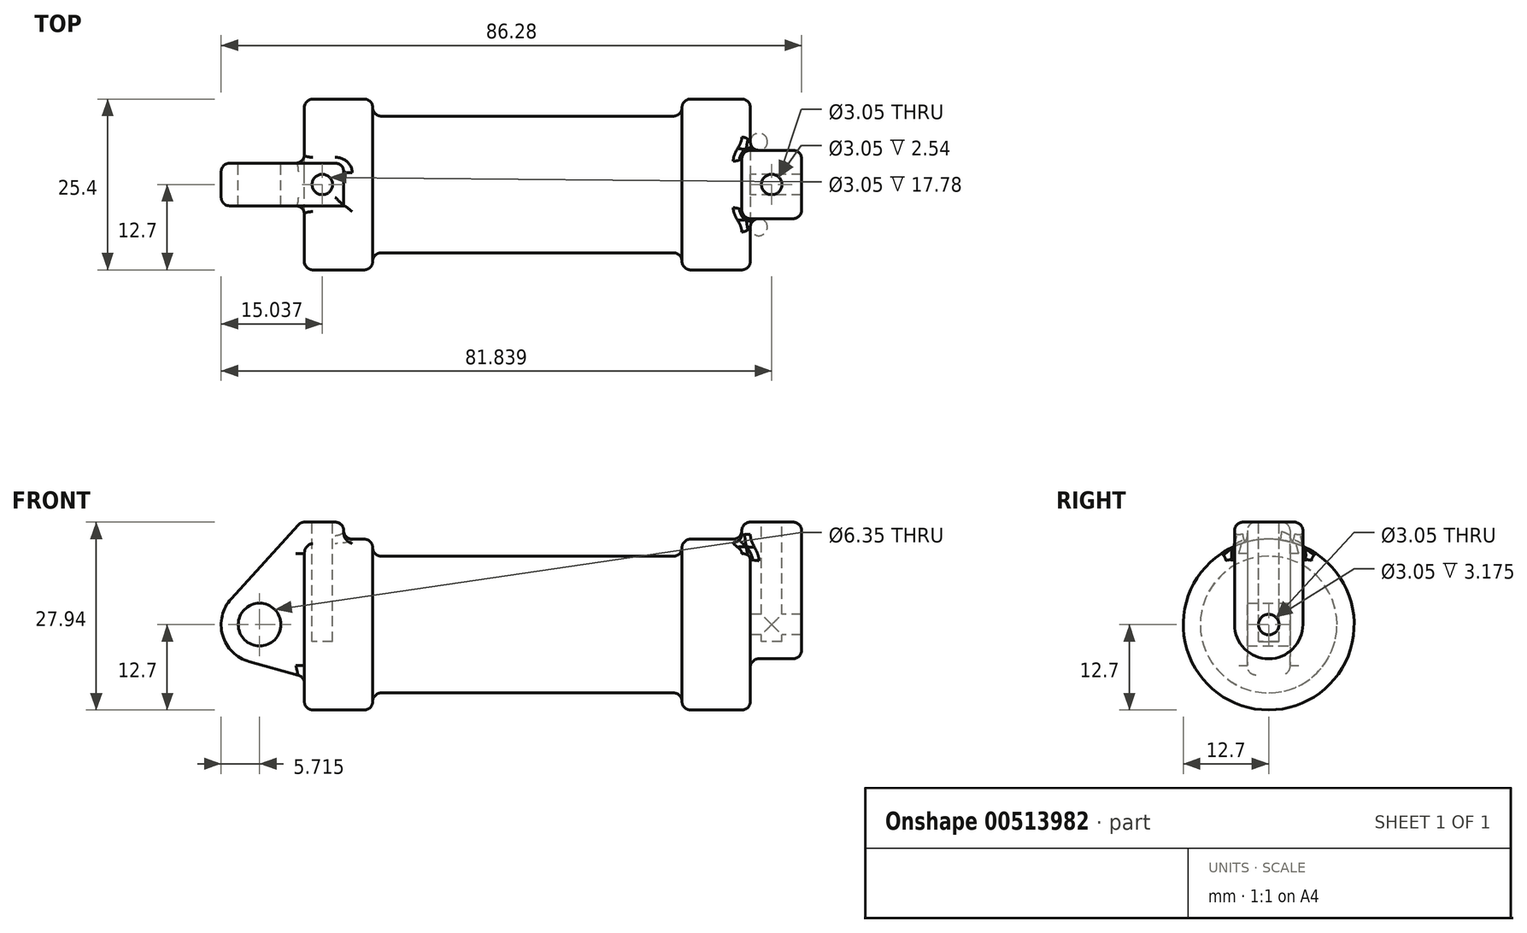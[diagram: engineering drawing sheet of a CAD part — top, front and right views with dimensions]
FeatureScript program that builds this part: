
annotation { "Feature Type Name" : "Feature", "Feature Type Description" : "" }
export const myFeature = defineFeature(function(context is Context, id is Id, definition is map)
    precondition{}
    {
        {
            var Q0;
            Q0=qCreatedBy(makeId("Front.planeOp"),FACE);
            var sketch = newSketch(context, id + "F0", { "sketchPlane" : qUnion([Q0])});
            skLineSegment(sketch, "E0", {"start": v(0, 0) * mm, "end": v(0, 12.7) * mm});
            skLineSegment(sketch, "E1", {"start": v(0, 12.7) * mm, "end": v(10.16, 12.7) * mm});
            skLineSegment(sketch, "E2", {"start": v(10.16, 12.7) * mm, "end": v(10.16, 10.16) * mm});
            skLineSegment(sketch, "E3", {"start": v(10.16, 10.16) * mm, "end": v(56.13, 10.16) * mm});
            skLineSegment(sketch, "E4", {"start": v(56.13, 10.16) * mm, "end": v(56.13, 12.7) * mm});
            skLineSegment(sketch, "E5", {"start": v(56.13, 12.7) * mm, "end": v(66.3, 12.7) * mm});
            skLineSegment(sketch, "E6", {"start": v(66.3, 12.7) * mm, "end": v(66.3, 0) * mm});
            skLineSegment(sketch, "E7", {"start": v(66.3, 0) * mm, "end": v(0, 0) * mm});
            skLineSegment(sketch, "E8", {"start": v(5.84, 15.24) * mm, "end": v(-0.5, 15.24) * mm});
            skLineSegment(sketch, "E9", {"start": v(-0.5, 15.24) * mm, "end": v(-10.88, 3.85) * mm});
            skLineSegment(sketch, "E10", {"start": v(0, 0) * mm, "end": v(-6.65, 0) * mm});
            skCircle(sketch, "E11", {"center": v(-6.65, 0) * mm, "radius": 5.72 * mm});
            skCircle(sketch, "E12", {"center": v(-6.65, 0) * mm, "radius": 3.18 * mm});
            skLineSegment(sketch, "E13", {"start": v(5.84, 15.24) * mm, "end": v(5.84, -9.4) * mm});
            skLineSegment(sketch, "E14", {"start": v(5.84, -9.4) * mm, "end": v(-8.18, -5.5) * mm});
            skSolve(sketch);
        }
        {
            var Q0;
            {var subQ0=sQuery(id+"F0.wireOp",EDGE,"E2");Q0=makeQuery(id+"F0.imprint","IMPRINT",FACE,{"disambiguationData":[TD([[makeQuery(id+"F0.imprint","IMPRINT",EDGE,{"derivedFrom":subQ0}),-1.0]])]});}
            var Q1;
            {var subQ0=sQuery(id+"F0.wireOp",EDGE,"E0");Q1=makeQuery(id+"F0.imprint","IMPRINT",FACE,{"disambiguationData":[TD([[makeQuery(id+"F0.imprint","IMPRINT",EDGE,{"derivedFrom":subQ0}),-1.0]])]});}
            var Q2;
            Q2=sQuery(id+"F0.wireOp",EDGE,"E7");
            revolve(context, id + "F1", {"entities" : qUnion([Q0, Q1]), "axis" : qUnion([Q2]), "revolveType" : RevolveType.FULL});
        }
        {
            var Q0;
            {var subQ1=sQuery(id+"F0.wireOp",EDGE,"E0");Q0=makeQuery(id+"F0.imprint","IMPRINT",FACE,{"disambiguationData":[TD([[makeQuery(id+"F0.imprint","IMPRINT",EDGE,{"derivedFrom":subQ1}),1.0]])]});}
            var Q1;
            {var subQ5=sQuery(id+"F0.wireOp",EDGE,"E12");Q1=makeQuery(id+"F0.imprint","IMPRINT",FACE,{"disambiguationData":[TD([[makeQuery(id+"F0.imprint","IMPRINT",EDGE,{"derivedFrom":subQ5}),-1.0]])]});}
            var Q2;
            {var subQ0=sQuery(id+"F0.wireOp",EDGE,"E14");Q2=makeQuery(id+"F0.imprint","IMPRINT",FACE,{"disambiguationData":[TD([[makeQuery(id+"F0.imprint","IMPRINT",EDGE,{"derivedFrom":subQ0}),-1.0]])]});}
            var Q3;
            {var subQ0=sQuery(id+"F0.wireOp",EDGE,"E0");Q3=makeQuery(id+"F0.imprint","IMPRINT",FACE,{"disambiguationData":[TD([[makeQuery(id+"F0.imprint","IMPRINT",EDGE,{"derivedFrom":subQ0}),-1.0]])]});}
            extrude(context, id + "F2", {"entities" : qUnion([Q0, Q1, Q2, Q3]), "operationType" : NewBodyOperationType.ADD, "endBound" : BoundingType.SYMMETRIC, "depth" : 6.35 * mm, "offsetDistance" : 25.4 * mm});
        }
        {
            var Q0;
            Q0=makeQuery(id+"F1.opRevolve","SWEPT_FACE",FACE,{"disambiguationData":[OSD([sQuery(id+"F0.wireOp",EDGE,"E6")])]});
            var sketch = newSketch(context, id + "F3", { "sketchPlane" : qUnion([Q0])});
            skCircle(sketch, "E15", {"center": v(0, 0) * mm, "radius": 1.52 * mm});
            skCircle(sketch, "E16", {"center": v(0, 0) * mm, "radius": 5.08 * mm});
            skLineSegment(sketch, "E17", {"start": v(5.08, 0) * mm, "end": v(5.08, 15.24) * mm});
            skLineSegment(sketch, "E18", {"start": v(-5.08, 0) * mm, "end": v(-5.08, 15.24) * mm});
            skLineSegment(sketch, "E19", {"start": v(-5.08, 15.24) * mm, "end": v(5.08, 15.24) * mm});
            skSolve(sketch);
        }
        {
            var Q0;
            Q0=makeQuery(id+"F3.imprint","IMPRINT",FACE,{"disambiguationData":[TD([[makeQuery(id+"F3.imprint","IMPRINT",EDGE,{"derivedFrom":sQuery(id+"F3.wireOp",EDGE,"E15")}),-1.0]])]});
            var Q1;
            {var subQ0=sQuery(id+"F3.wireOp",EDGE,"E17");var subQ1=sQuery(id+"F3.wireOp",EDGE,"E16");var subQ2=makeQuery(id+"F3.imprint","INTERSECT",VERTEX,{"derivedFrom":[subQ1,subQ0]});Q1=makeQuery(id+"F3.imprint","IMPRINT",FACE,{"disambiguationData":[TD([[makeQuery(id+"F3.imprint","IMPRINT",EDGE,{"disambiguationData":[TD([[subQ2,-1.0]])],"derivedFrom":subQ1}),-1.0]])]});}
            var Q2;
            {var subQ0=sQuery(id+"F3.wireOp",EDGE,"E19");Q2=makeQuery(id+"F3.imprint","IMPRINT",FACE,{"disambiguationData":[TD([[makeQuery(id+"F3.imprint","IMPRINT",EDGE,{"derivedFrom":subQ0}),-1.0]])]});}
            extrude(context, id + "F4", {"entities" : qUnion([Q0, Q1, Q2]), "operationType" : NewBodyOperationType.ADD, "depth" : 7.62 * mm, "hasSecondDirection" : true, "secondDirectionOppositeDirection" : true, "secondDirectionDepth" : 1.27 * mm});
        }
        {
            var Q0;
            Q0=makeQuery(id+"F2.opExtrude","SWEPT_FACE",FACE,{"disambiguationData":[OSD([sQuery(id+"F0.wireOp",EDGE,"E8")])]});
            var sketch = newSketch(context, id + "F5", { "sketchPlane" : qUnion([Q0])});
            skCircle(sketch, "E20", {"center": v(2.67, 0) * mm, "radius": 1.52 * mm});
            skPoint(sketch, "E21.0", {"position": v(65.02, 0) * mm});
            skPoint(sketch, "E22.0", {"position": v(69.47, 5.08) * mm});
            skCircle(sketch, "E23", {"center": v(69.47, 0) * mm, "radius": 1.52 * mm});
            skSolve(sketch);
        }
        {
            var Q0;
            Q0=makeQuery(id+"F5.imprint","IMPRINT",FACE,{"disambiguationData":[TD([[makeQuery(id+"F5.imprint","IMPRINT",EDGE,{"derivedFrom":sQuery(id+"F5.wireOp",EDGE,"E23")}),1.0]])]});
            var Q1;
            Q1=sQuery(id+"F5.wireOp",EDGE,"E20");
            extrude(context, id + "F6", {"entities" : qUnion([Q0]), "operationType" : NewBodyOperationType.REMOVE, "surfaceEntities" : qUnion([Q1]), "oppositeDirection" : true, "depth" : 10.4 * mm});
        }
        {
            var Q0;
            Q0 = qSketchRegion(id + "F5", true);
            extrude(context, id + "F7", {"entities" : qUnion([Q0]), "operationType" : NewBodyOperationType.REMOVE, "oppositeDirection" : true, "depth" : 17.78 * mm});
        }
        {
            var Q0;
            Q0=makeQuery(id+"F1.opRevolve","SWEPT_FACE",FACE,{"disambiguationData":[OSD([sQuery(id+"F0.wireOp",EDGE,"E4")])]});
            fillet(context, id + "F8", {"entities" : qUnion([Q0]), "radius" : 1.27 * mm, "tangentPropagation" : true, "allowEdgeOverflow" : false});
        }
        {
            var Q0;
            Q0=makeQuery(id+"F1.opRevolve","SWEPT_FACE",FACE,{"disambiguationData":[OSD([sQuery(id+"F0.wireOp",EDGE,"E2")])]});
            fillet(context, id + "F9", {"entities" : qUnion([Q0]), "radius" : 1.27 * mm, "tangentPropagation" : true, "allowEdgeOverflow" : false});
        }
        {
            var Q0;
            Q0=makeQuery(id+"F1.opRevolve","SWEPT_EDGE",EDGE,{"disambiguationData":[OSD([sQuery(id+"F0.wireOp",EDGE,"E0"),sQuery(id+"F0.wireOp",EDGE,"E1")])]});
            var Q1;
            Q1=makeQuery(id+"F2.boolean.opBoolean","INTERSECT",EDGE,{"derivedFrom":[makeQuery(id+"F1.opRevolve","SWEPT_FACE",FACE,{"disambiguationData":[OSD([sQuery(id+"F0.wireOp",EDGE,"E0")])]}),makeQuery(id+"F2.opExtrude","CAP_FACE",FACE,{"disambiguationData":[OSD([sQuery(id+"F0.wireOp",EDGE,"E8"),sQuery(id+"F0.wireOp",EDGE,"E9"),sQuery(id+"F0.wireOp",EDGE,"E11"),sQuery(id+"F0.wireOp",EDGE,"E12"),sQuery(id+"F0.wireOp",EDGE,"E13"),sQuery(id+"F0.wireOp",EDGE,"E14")])],"isStart":true})]});
            var Q2;
            {var subQ0=sQuery(id+"F0.wireOp",EDGE,"E1");Q2=makeQuery(id+"F9.opFillet","BLEND_EDGE",EDGE,{"blendedFrom":[makeQuery(id+"F1.opRevolve","SWEPT_EDGE",EDGE,{"disambiguationData":[OSD([subQ0,sQuery(id+"F0.wireOp",EDGE,"E2")])]}),makeQuery(id+"F1.opRevolve","SWEPT_FACE",FACE,{"disambiguationData":[OSD([subQ0])]})],"blendedInto":[makeQuery(id+"F1.opRevolve","SWEPT_FACE",FACE,{"disambiguationData":[OSD([subQ0])]})]});}
            var Q3;
            Q3=makeQuery(id+"F1.opRevolve","SWEPT_FACE",FACE,{"disambiguationData":[OSD([sQuery(id+"F0.wireOp",EDGE,"E1")])]});
            var Q4;
            Q4=makeQuery(id+"F2.opExtrude","CAP_EDGE",EDGE,{"disambiguationData":[OSD([sQuery(id+"F0.wireOp",EDGE,"E13")])],"isStart":true});
            var Q5;
            Q5=makeQuery(id+"F2.boolean.opBoolean","INTERSECT",EDGE,{"derivedFrom":[makeQuery(id+"F1.opRevolve","SWEPT_FACE",FACE,{"disambiguationData":[OSD([sQuery(id+"F0.wireOp",EDGE,"E1")])]}),makeQuery(id+"F2.opExtrude","CAP_FACE",FACE,{"disambiguationData":[OSD([sQuery(id+"F0.wireOp",EDGE,"E8"),sQuery(id+"F0.wireOp",EDGE,"E9"),sQuery(id+"F0.wireOp",EDGE,"E11"),sQuery(id+"F0.wireOp",EDGE,"E12"),sQuery(id+"F0.wireOp",EDGE,"E13"),sQuery(id+"F0.wireOp",EDGE,"E14")])],"isStart":true})]});
            var Q6;
            Q6=makeQuery(id+"F2.opExtrude","CAP_EDGE",EDGE,{"disambiguationData":[OSD([sQuery(id+"F0.wireOp",EDGE,"E8")])],"isStart":true});
            var Q7;
            Q7=makeQuery(id+"F2.opExtrude","CAP_EDGE",EDGE,{"disambiguationData":[OSD([sQuery(id+"F0.wireOp",EDGE,"E9")])],"isStart":true});
            var Q8;
            Q8=makeQuery(id+"F2.opExtrude","CAP_EDGE",EDGE,{"disambiguationData":[OSD([sQuery(id+"F0.wireOp",EDGE,"E11")])],"isStart":true});
            var Q9;
            Q9=makeQuery(id+"F2.opExtrude","SWEPT_EDGE",EDGE,{"disambiguationData":[OSD([sQuery(id+"F0.wireOp",EDGE,"E9"),sQuery(id+"F0.wireOp",EDGE,"E11")])]});
            var Q10;
            Q10=makeQuery(id+"F2.opExtrude","CAP_EDGE",EDGE,{"disambiguationData":[OSD([sQuery(id+"F0.wireOp",EDGE,"E9")])],"isStart":false});
            var Q11;
            Q11=makeQuery(id+"F2.opExtrude","SWEPT_EDGE",EDGE,{"disambiguationData":[OSD([sQuery(id+"F0.wireOp",EDGE,"E8"),sQuery(id+"F0.wireOp",EDGE,"E9")])]});
            var Q12;
            Q12=makeQuery(id+"F2.opExtrude","CAP_EDGE",EDGE,{"disambiguationData":[OSD([sQuery(id+"F0.wireOp",EDGE,"E8")])],"isStart":false});
            var Q13;
            Q13=makeQuery(id+"F2.opExtrude","SWEPT_EDGE",EDGE,{"disambiguationData":[OSD([sQuery(id+"F0.wireOp",EDGE,"E8"),sQuery(id+"F0.wireOp",EDGE,"E13")])]});
            var Q14;
            Q14=makeQuery(id+"F2.opExtrude","CAP_EDGE",EDGE,{"disambiguationData":[OSD([sQuery(id+"F0.wireOp",EDGE,"E11")])],"isStart":false});
            var Q15;
            Q15=makeQuery(id+"F2.opExtrude","CAP_EDGE",EDGE,{"disambiguationData":[OSD([sQuery(id+"F0.wireOp",EDGE,"E14")])],"isStart":false});
            var Q16;
            Q16=makeQuery(id+"F2.boolean.opBoolean","INTERSECT",EDGE,{"derivedFrom":[makeQuery(id+"F1.opRevolve","SWEPT_FACE",FACE,{"disambiguationData":[OSD([sQuery(id+"F0.wireOp",EDGE,"E0")])]}),makeQuery(id+"F2.opExtrude","CAP_FACE",FACE,{"disambiguationData":[OSD([sQuery(id+"F0.wireOp",EDGE,"E8"),sQuery(id+"F0.wireOp",EDGE,"E9"),sQuery(id+"F0.wireOp",EDGE,"E11"),sQuery(id+"F0.wireOp",EDGE,"E12"),sQuery(id+"F0.wireOp",EDGE,"E13"),sQuery(id+"F0.wireOp",EDGE,"E14")])],"isStart":false})]});
            var Q17;
            Q17=makeQuery(id+"F2.opExtrude","CAP_EDGE",EDGE,{"disambiguationData":[OSD([sQuery(id+"F0.wireOp",EDGE,"E14")])],"isStart":true});
            var Q18;
            Q18=makeQuery(id+"F2.boolean.opBoolean","INTERSECT",EDGE,{"derivedFrom":[makeQuery(id+"F1.opRevolve","SWEPT_FACE",FACE,{"disambiguationData":[OSD([sQuery(id+"F0.wireOp",EDGE,"E0")])]}),makeQuery(id+"F2.opExtrude","SWEPT_FACE",FACE,{"disambiguationData":[OSD([sQuery(id+"F0.wireOp",EDGE,"E14")])]})]});
            fillet(context, id + "F10", {"entities" : qUnion([Q0, Q1, Q2, Q3, Q4, Q5, Q6, Q7, Q8, Q9, Q10, Q11, Q12, Q13, Q14, Q15, Q16, Q17, Q18]), "radius" : 1.27 * mm, "tangentPropagation" : true, "allowEdgeOverflow" : false});
        }
        {
            var Q0;
            Q0=makeQuery(id+"F4.opExtrude","SWEPT_EDGE",EDGE,{"disambiguationData":[OSD([sQuery(id+"F3.wireOp",EDGE,"E17"),sQuery(id+"F3.wireOp",EDGE,"E19")])]});
            var Q1;
            Q1=makeQuery(id+"F4.opExtrude","SWEPT_EDGE",EDGE,{"disambiguationData":[OSD([sQuery(id+"F3.wireOp",EDGE,"E18"),sQuery(id+"F3.wireOp",EDGE,"E19")])]});
            var Q2;
            Q2=makeQuery(id+"F4.opExtrude","CAP_EDGE",EDGE,{"disambiguationData":[OSD([sQuery(id+"F3.wireOp",EDGE,"E19")])],"isStart":false});
            var Q3;
            Q3=makeQuery(id+"F4.opExtrude","CAP_EDGE",EDGE,{"disambiguationData":[OSD([sQuery(id+"F3.wireOp",EDGE,"E19")])],"isStart":true});
            var Q4;
            Q4=makeQuery(id+"F4.opExtrude","CAP_EDGE",EDGE,{"disambiguationData":[OSD([sQuery(id+"F3.wireOp",EDGE,"E17")])],"isStart":true});
            var Q5;
            Q5=makeQuery(id+"F4.boolean.opBoolean","INTERSECT",EDGE,{"derivedFrom":[makeQuery(id+"F1.opRevolve","SWEPT_FACE",FACE,{"disambiguationData":[OSD([sQuery(id+"F0.wireOp",EDGE,"E5")])]}),makeQuery(id+"F4.opExtrude","CAP_FACE",FACE,{"disambiguationData":[OSD([sQuery(id+"F3.wireOp",EDGE,"E15"),sQuery(id+"F3.wireOp",EDGE,"E16"),sQuery(id+"F3.wireOp",EDGE,"E17"),sQuery(id+"F3.wireOp",EDGE,"E18"),sQuery(id+"F3.wireOp",EDGE,"E19")])],"isStart":true})]});
            var Q6;
            Q6=makeQuery(id+"F4.opExtrude","CAP_EDGE",EDGE,{"disambiguationData":[OSD([sQuery(id+"F3.wireOp",EDGE,"E18")])],"isStart":true});
            var Q7;
            Q7=makeQuery(id+"F4.opExtrude","CAP_EDGE",EDGE,{"disambiguationData":[OSD([sQuery(id+"F3.wireOp",EDGE,"E17")])],"isStart":false});
            var Q8;
            Q8=makeQuery(id+"F4.opExtrude","CAP_EDGE",EDGE,{"disambiguationData":[OSD([sQuery(id+"F3.wireOp",EDGE,"E18")])],"isStart":false});
            var Q9;
            Q9=makeQuery(id+"F4.opExtrude","CAP_EDGE",EDGE,{"disambiguationData":[OSD([sQuery(id+"F3.wireOp",EDGE,"E16")])],"isStart":false});
            var Q10;
            Q10=makeQuery(id+"F4.boolean.opBoolean","INTERSECT",EDGE,{"derivedFrom":[makeQuery(id+"F1.opRevolve","SWEPT_FACE",FACE,{"disambiguationData":[OSD([sQuery(id+"F0.wireOp",EDGE,"E6")])]}),makeQuery(id+"F4.opExtrude","SWEPT_FACE",FACE,{"disambiguationData":[OSD([sQuery(id+"F3.wireOp",EDGE,"E16")])]})]});
            var Q11;
            Q11=makeQuery(id+"F4.opExtrude","SWEPT_EDGE",EDGE,{"disambiguationData":[OSD([sQuery(id+"F3.wireOp",EDGE,"E16"),sQuery(id+"F3.wireOp",EDGE,"E17")])]});
            var Q12;
            Q12=makeQuery(id+"F4.opExtrude","SWEPT_EDGE",EDGE,{"disambiguationData":[OSD([sQuery(id+"F3.wireOp",EDGE,"E16"),sQuery(id+"F3.wireOp",EDGE,"E18")])]});
            var Q13;
            Q13=makeQuery(id+"F1.opRevolve","SWEPT_EDGE",EDGE,{"disambiguationData":[OSD([sQuery(id+"F0.wireOp",EDGE,"E5"),sQuery(id+"F0.wireOp",EDGE,"E6")])]});
            var Q14;
            Q14=makeQuery(id+"F1.opRevolve","SWEPT_FACE",FACE,{"disambiguationData":[OSD([sQuery(id+"F0.wireOp",EDGE,"E5")])]});
            fillet(context, id + "F11", {"entities" : qUnion([Q0, Q1, Q2, Q3, Q4, Q5, Q6, Q7, Q8, Q9, Q10, Q11, Q12, Q13, Q14]), "radius" : 1.27 * mm, "tangentPropagation" : true, "allowEdgeOverflow" : false});
        }
    });
